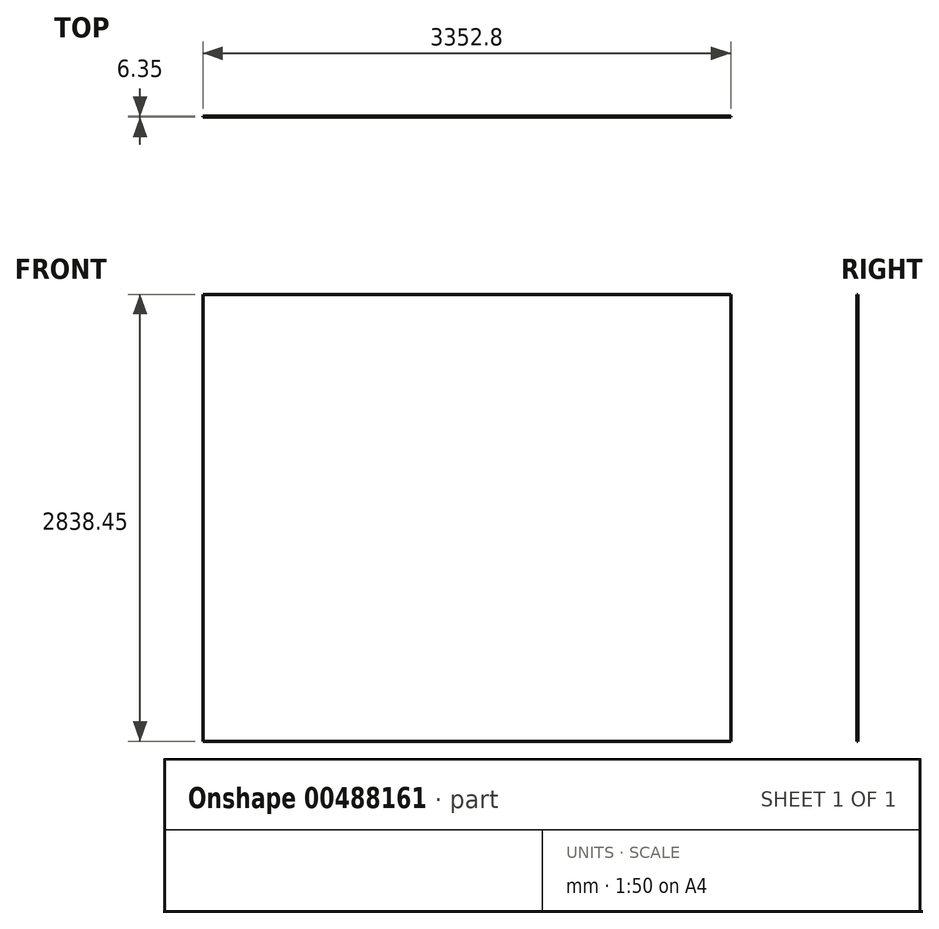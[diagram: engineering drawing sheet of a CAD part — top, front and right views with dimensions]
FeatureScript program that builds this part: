
annotation { "Feature Type Name" : "Feature", "Feature Type Description" : "" }
export const myFeature = defineFeature(function(context is Context, id is Id, definition is map)
    precondition{}
    {
        {
            var Q0;
            Q0=qCreatedBy(makeId("Front.planeOp"),FACE);
            var sketch = newSketch(context, id + "F0", { "sketchPlane" : qUnion([Q0])});
            skLineSegment(sketch, "E0", {"start": v(0, 2838.45) * mm, "end": v(3352.8, 2838.45) * mm});
            skLineSegment(sketch, "E1", {"start": v(3352.8, 2838.45) * mm, "end": v(3352.8, 0) * mm});
            skLineSegment(sketch, "E2", {"start": v(3352.8, 0) * mm, "end": v(0, 0) * mm});
            skLineSegment(sketch, "E3", {"start": v(0, 2838.45) * mm, "end": v(0, 0) * mm});
            skSolve(sketch);
        }
        {
            var Q0;
            Q0=makeQuery(id+"F0.imprint","IMPRINT",FACE,{"disambiguationData":[TD([[makeQuery(id+"F0.imprint","IMPRINT",EDGE,{"derivedFrom":sQuery(id+"F0.wireOp",EDGE,"E0")}),-1.0]])]});
            extrude(context, id + "F1", {"entities" : qUnion([Q0]), "depth" : 6.35 * mm, "offsetDistance" : 25.4 * mm});
        }
    });
